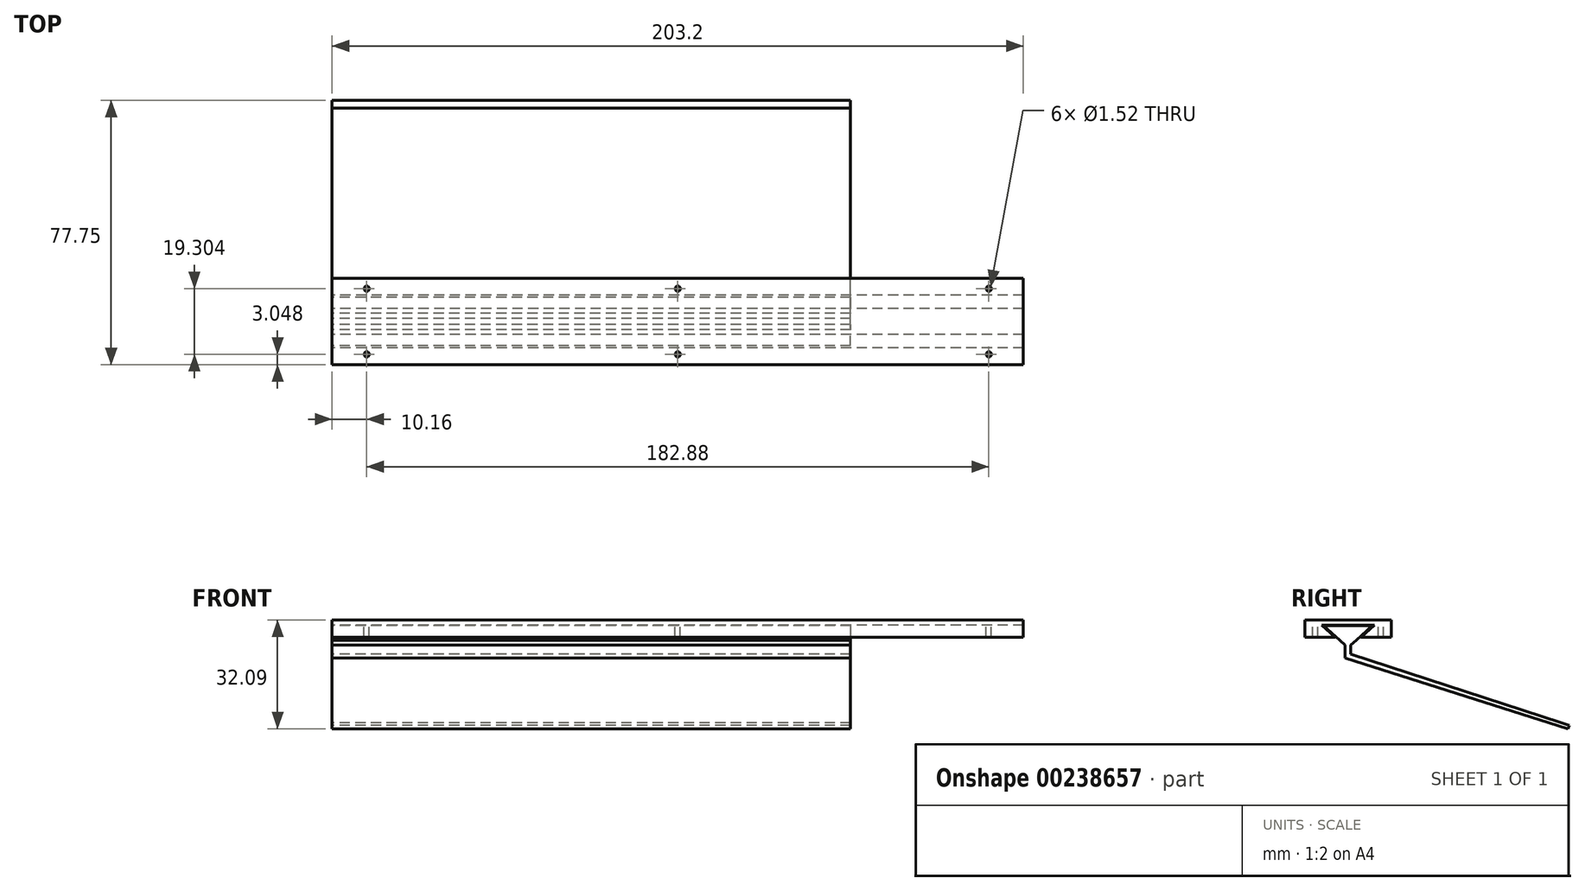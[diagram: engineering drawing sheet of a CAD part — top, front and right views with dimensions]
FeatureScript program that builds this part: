
annotation { "Feature Type Name" : "Feature", "Feature Type Description" : "" }
export const myFeature = defineFeature(function(context is Context, id is Id, definition is map)
    precondition{}
    {
        {
            var Q0;
            Q0=qCreatedBy(makeId("Right.planeOp"),FACE);
            var sketch = newSketch(context, id + "F0", { "sketchPlane" : qUnion([Q0])});
            skLineSegment(sketch, "E0", {"start": v(0, 7.7) * mm, "end": v(-12.7, 7.7) * mm});
            skLineSegment(sketch, "E1", {"start": v(-12.7, 7.7) * mm, "end": v(-12.7, 2.61) * mm});
            skLineSegment(sketch, "E2", {"start": v(-12.7, 2.61) * mm, "end": v(-3.81, 2.61) * mm});
            skLineSegment(sketch, "E3", {"start": v(-3.81, 2.61) * mm, "end": v(-7.78, 6.17) * mm});
            skLineSegment(sketch, "E4", {"start": v(-7.78, 6.17) * mm, "end": v(0, 6.17) * mm});
            skLineSegment(sketch, "E5.MirrorCS", {"start": v(0, 7.7) * mm, "end": v(12.7, 7.7) * mm});
            skLineSegment(sketch, "E6.MirrorCS", {"start": v(12.7, 7.7) * mm, "end": v(12.7, 2.61) * mm});
            skLineSegment(sketch, "E7.MirrorCS", {"start": v(12.7, 2.61) * mm, "end": v(3.81, 2.61) * mm});
            skLineSegment(sketch, "E8.MirrorCS", {"start": v(3.8, 2.61) * mm, "end": v(7.78, 6.17) * mm});
            skLineSegment(sketch, "E9.MirrorCS", {"start": v(7.78, 6.17) * mm, "end": v(0, 6.17) * mm});
            skSolve(sketch);
        }
        {
            var Q0;
            Q0=makeQuery(id+"F0.imprint","IMPRINT",FACE,{"disambiguationData":[TD([[makeQuery(id+"F0.imprint","IMPRINT",EDGE,{"derivedFrom":sQuery(id+"F0.wireOp",EDGE,"E0")}),1.0]])]});
            extrude(context, id + "F1", {"entities" : qUnion([Q0]), "depth" : 203.2 * mm});
        }
        {
            var Q0;
            Q0=makeQuery(id+"F1.opExtrude","SWEPT_FACE",FACE,{"disambiguationData":[OSD([sQuery(id+"F0.wireOp",EDGE,"E0"),sQuery(id+"F0.wireOp",EDGE,"E5.MirrorCS")])]});
            var sketch = newSketch(context, id + "F2", { "sketchPlane" : qUnion([Q0])});
            skCircle(sketch, "E10", {"center": v(101.6, 9.65) * mm, "radius": 1.02 * mm});
            skPoint(sketch, "E10.centerSnap0", {"position": v(101.6, 12.7) * mm});
            skCircle(sketch, "E11", {"center": v(101.6, -9.65) * mm, "radius": 1.02 * mm});
            skPoint(sketch, "E11.centerSnap0", {"position": v(101.6, -12.7) * mm});
            skCircle(sketch, "E12", {"center": v(10.16, -9.65) * mm, "radius": 1.02 * mm});
            skCircle(sketch, "E13", {"center": v(10.16, 9.65) * mm, "radius": 1.02 * mm});
            skCircle(sketch, "E14", {"center": v(193.04, 9.65) * mm, "radius": 1.02 * mm});
            skCircle(sketch, "E15", {"center": v(193.04, -9.65) * mm, "radius": 1.02 * mm});
            skSolve(sketch);
        }
        {
            var Q0;
            Q0=sQuery(id+"F2.wireOp",VERTEX,"E10.center");
            var Q1;
            Q1=sQuery(id+"F2.wireOp",VERTEX,"E11.center");
            var Q2;
            Q2=sQuery(id+"F2.wireOp",VERTEX,"E13.center");
            var Q3;
            Q3=sQuery(id+"F2.wireOp",VERTEX,"E12.center");
            var Q4;
            Q4=sQuery(id+"F2.wireOp",VERTEX,"E14.center");
            var Q5;
            Q5=sQuery(id+"F2.wireOp",VERTEX,"E15.center");
            var Q6;
            Q6=makeQuery(id+"F1.opExtrude","SWEPT_BODY",BODY,{"disambiguationData":[OSD([sQuery(id+"F0.wireOp",EDGE,"E0"),sQuery(id+"F0.wireOp",EDGE,"E1"),sQuery(id+"F0.wireOp",EDGE,"E2"),sQuery(id+"F0.wireOp",EDGE,"E3"),sQuery(id+"F0.wireOp",EDGE,"E4"),sQuery(id+"F0.wireOp",EDGE,"E5.MirrorCS"),sQuery(id+"F0.wireOp",EDGE,"E6.MirrorCS"),sQuery(id+"F0.wireOp",EDGE,"E7.MirrorCS"),sQuery(id+"F0.wireOp",EDGE,"E8.MirrorCS"),sQuery(id+"F0.wireOp",EDGE,"E9.MirrorCS")])]});
            hole(context, id + "F3", {"style" : HoleStyle.SIMPLE, "endStyle" : HoleEndStyle.THROUGH, "holeDiameter" : 1.52 * mm, "locations" : qUnion([Q0, Q1, Q2, Q3, Q4, Q5]), "scope" : qUnion([Q6]), "isTappedThrough" : true});
        }
        {
            var Q0;
            Q0=qCreatedBy(makeId("Right.planeOp"),FACE);
            var sketch = newSketch(context, id + "F4", { "sketchPlane" : qUnion([Q0])});
            skLineSegment(sketch, "E16", {"start": v(0, 5.97) * mm, "end": v(-7.17, 5.97) * mm});
            skLineSegment(sketch, "E17", {"start": v(-7.17, 5.97) * mm, "end": v(-3.74, 2.88) * mm});
            skLineSegment(sketch, "E18", {"start": v(-3.74, 2.88) * mm, "end": v(-2.43, 1.7) * mm});
            skLineSegment(sketch, "E19", {"start": v(-0.86, 0.2) * mm, "end": v(-2.43, 1.7) * mm});
            skLineSegment(sketch, "E20", {"start": v(-0.86, 0.2) * mm, "end": v(-0.86, -3.52) * mm});
            skLineSegment(sketch, "E21", {"start": v(-0.86, -27.05) * mm, "end": v(0, -27.05) * mm});
            skLineSegment(sketch, "E22.MirrorCS", {"start": v(0, 5.97) * mm, "end": v(7.17, 5.97) * mm});
            skLineSegment(sketch, "E23.MirrorCS", {"start": v(7.17, 5.97) * mm, "end": v(3.74, 2.88) * mm});
            skLineSegment(sketch, "E24.MirrorCS", {"start": v(3.74, 2.88) * mm, "end": v(2.43, 1.7) * mm});
            skLineSegment(sketch, "E25.MirrorCS", {"start": v(0.86, 0.2) * mm, "end": v(2.43, 1.7) * mm});
            skLineSegment(sketch, "E26.MirrorCS", {"start": v(0.86, 0.2) * mm, "end": v(0.86, -2.43) * mm});
            skLineSegment(sketch, "E27.MirrorCS", {"start": v(0.86, -27.05) * mm, "end": v(0, -27.05) * mm});
            skLineSegment(sketch, "E28", {"start": v(0.86, -27.05) * mm, "end": v(64.34, -27.05) * mm, "construction": true});
            skLineSegment(sketch, "E29", {"start": v(62.79, 2.6) * mm, "end": v(62.79, -23.61) * mm, "construction": true});
            skLineSegment(sketch, "E30", {"start": v(0.86, -2.43) * mm, "end": v(62.79, -22.54) * mm});
            skLineSegment(sketch, "E31", {"start": v(-0.86, -3.52) * mm, "end": v(62.29, -23.63) * mm});
            skLineSegment(sketch, "E32", {"start": v(62.29, -23.63) * mm, "end": v(64.72, -24.4) * mm});
            skLineSegment(sketch, "E33", {"start": v(64.72, -24.4) * mm, "end": v(65.05, -23.38) * mm});
            skLineSegment(sketch, "E34", {"start": v(65.05, -23.38) * mm, "end": v(62.79, -22.54) * mm});
            skSolve(sketch);
        }
        {
            var Q0;
            Q0=makeQuery(id+"F4.imprint","IMPRINT",FACE,{"disambiguationData":[TD([[makeQuery(id+"F4.imprint","IMPRINT",EDGE,{"derivedFrom":sQuery(id+"F4.wireOp",EDGE,"E16")}),1.0]])]});
            extrude(context, id + "F5", {"entities" : qUnion([Q0]), "depth" : 152.4 * mm});
        }
    });
